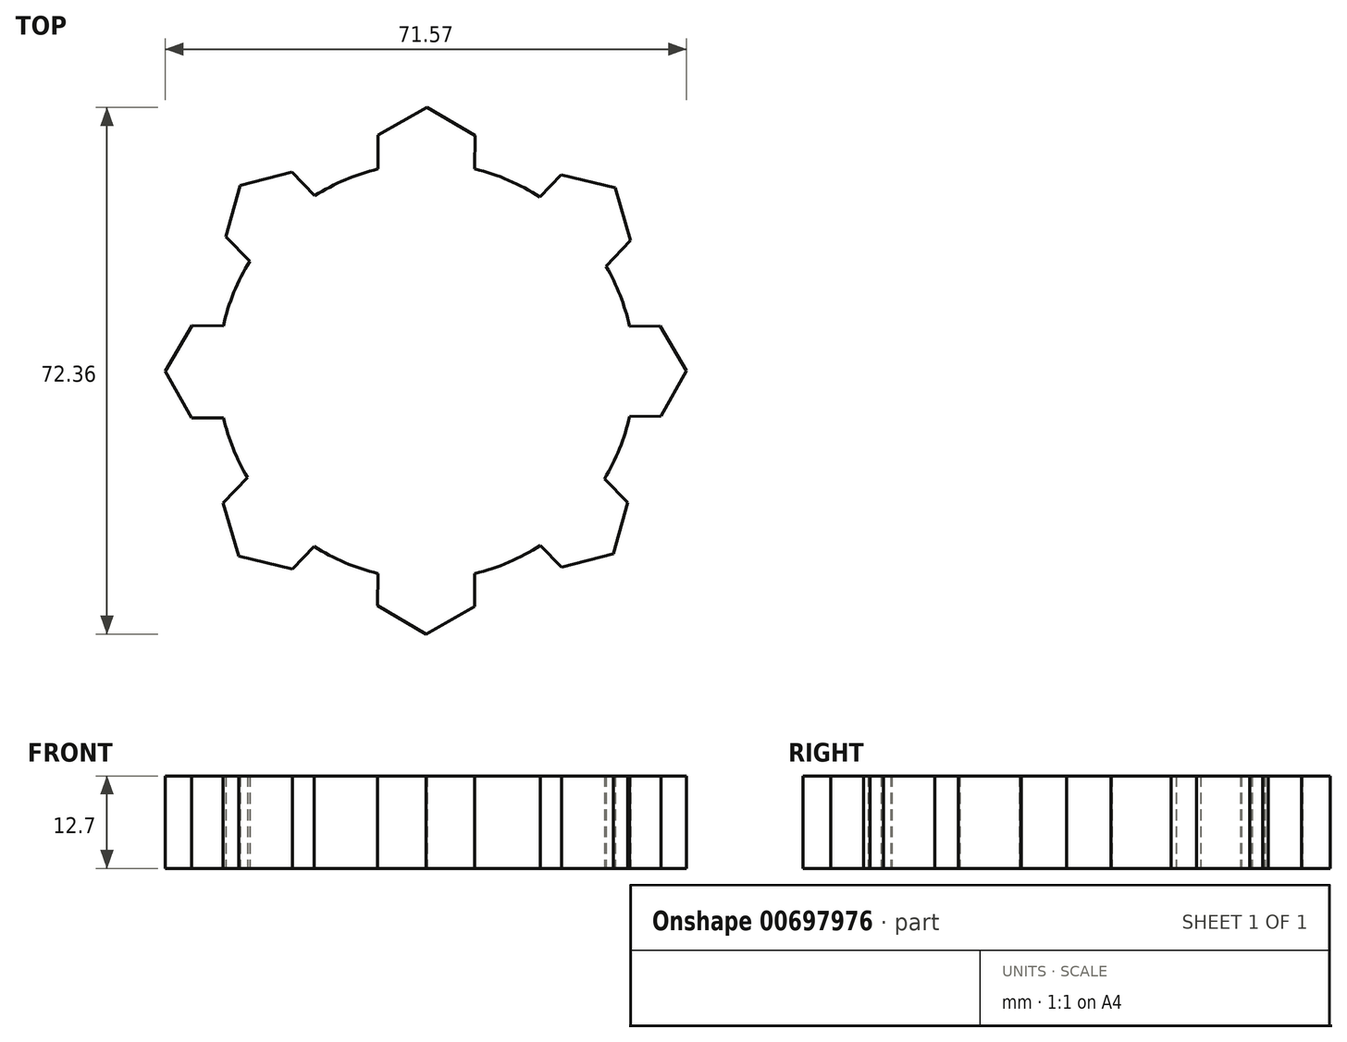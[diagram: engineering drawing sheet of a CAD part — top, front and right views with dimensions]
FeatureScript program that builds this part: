
annotation { "Feature Type Name" : "Feature", "Feature Type Description" : "" }
export const myFeature = defineFeature(function(context is Context, id is Id, definition is map)
    precondition{}
    {
        {
            var Q0;
            Q0=qCreatedBy(makeId("Top.planeOp"),FACE);
            var sketch = newSketch(context, id + "F0", { "sketchPlane" : qUnion([Q0])});
            skCircle(sketch, "E0", {"center": v(0, 0) * mm, "radius": 28.58 * mm});
            skCircle(sketch, "E1.cCircle", {"center": v(0, 28.58) * mm, "radius": 6.65 * mm, "construction": true});
            skLineSegment(sketch, "E1.0", {"start": v(0.06, 36.25) * mm, "end": v(6.68, 32.36) * mm});
            skLineSegment(sketch, "E1.1", {"start": v(6.68, 32.36) * mm, "end": v(6.62, 24.68) * mm});
            skLineSegment(sketch, "E1.2", {"start": v(6.62, 24.68) * mm, "end": v(-0.06, 20.9) * mm});
            skLineSegment(sketch, "E1.3", {"start": v(-0.06, 20.9) * mm, "end": v(-6.68, 24.8) * mm});
            skLineSegment(sketch, "E1.4", {"start": v(-6.68, 24.8) * mm, "end": v(-6.62, 32.47) * mm});
            skLineSegment(sketch, "E1.5", {"start": v(-6.62, 32.47) * mm, "end": v(0.06, 36.25) * mm});
            skPoint(sketch, "E1.0.midPoint", {"position": v(3.37, 34.3) * mm});
            skCircle(sketch, "E2.cCircle", {"center": v(0, -28.43) * mm, "radius": 6.65 * mm, "construction": true});
            skLineSegment(sketch, "E2.0", {"start": v(0.06, -20.75) * mm, "end": v(6.68, -24.64) * mm});
            skLineSegment(sketch, "E2.1", {"start": v(6.68, -24.64) * mm, "end": v(6.62, -32.32) * mm});
            skLineSegment(sketch, "E2.2", {"start": v(6.62, -32.32) * mm, "end": v(-0.06, -36.1) * mm});
            skLineSegment(sketch, "E2.3", {"start": v(-0.06, -36.1) * mm, "end": v(-6.68, -32.21) * mm});
            skLineSegment(sketch, "E2.4", {"start": v(-6.68, -32.21) * mm, "end": v(-6.62, -24.53) * mm});
            skLineSegment(sketch, "E2.5", {"start": v(-6.62, -24.53) * mm, "end": v(0.06, -20.75) * mm});
            skPoint(sketch, "E2.0.midPoint", {"position": v(3.37, -22.7) * mm});
            skCircle(sketch, "E3.cCircle", {"center": v(-28.55, -0.08) * mm, "radius": 6.33 * mm, "construction": true});
            skLineSegment(sketch, "E3.0", {"start": v(-21.24, -0.14) * mm, "end": v(-24.95, -6.44) * mm});
            skLineSegment(sketch, "E3.1", {"start": v(-24.95, -6.44) * mm, "end": v(-32.26, -6.38) * mm});
            skLineSegment(sketch, "E3.2", {"start": v(-32.26, -6.38) * mm, "end": v(-35.86, -0.01) * mm});
            skLineSegment(sketch, "E3.3", {"start": v(-35.86, -0.01) * mm, "end": v(-32.15, 6.28) * mm});
            skLineSegment(sketch, "E3.4", {"start": v(-32.15, 6.28) * mm, "end": v(-24.84, 6.22) * mm});
            skLineSegment(sketch, "E3.5", {"start": v(-24.84, 6.22) * mm, "end": v(-21.24, -0.14) * mm});
            skCircle(sketch, "E4.cCircle", {"center": v(28.58, 0) * mm, "radius": 6.18 * mm, "construction": true});
            skLineSegment(sketch, "E4.0", {"start": v(35.71, 0.06) * mm, "end": v(32.2, -6.15) * mm});
            skLineSegment(sketch, "E4.1", {"start": v(32.2, -6.15) * mm, "end": v(25.05, -6.21) * mm});
            skLineSegment(sketch, "E4.2", {"start": v(25.05, -6.21) * mm, "end": v(21.44, -0.06) * mm});
            skLineSegment(sketch, "E4.3", {"start": v(21.44, -0.06) * mm, "end": v(24.96, 6.15) * mm});
            skLineSegment(sketch, "E4.4", {"start": v(24.96, 6.15) * mm, "end": v(32.1, 6.21) * mm});
            skLineSegment(sketch, "E4.5", {"start": v(32.1, 6.21) * mm, "end": v(35.71, 0.06) * mm});
            skCircle(sketch, "E5.cCircle", {"center": v(20.66, 19.74) * mm, "radius": 6.57 * mm, "construction": true});
            skLineSegment(sketch, "E5.0", {"start": v(25.9, 25.23) * mm, "end": v(28.04, 17.95) * mm});
            skLineSegment(sketch, "E5.1", {"start": v(28.04, 17.95) * mm, "end": v(22.8, 12.46) * mm});
            skLineSegment(sketch, "E5.2", {"start": v(22.8, 12.46) * mm, "end": v(15.43, 14.24) * mm});
            skLineSegment(sketch, "E5.3", {"start": v(15.43, 14.24) * mm, "end": v(13.29, 21.53) * mm});
            skLineSegment(sketch, "E5.4", {"start": v(13.29, 21.53) * mm, "end": v(18.53, 27.02) * mm});
            skLineSegment(sketch, "E5.5", {"start": v(18.53, 27.02) * mm, "end": v(25.9, 25.23) * mm});
            skCircle(sketch, "E6.cCircle", {"center": v(20.54, -19.87) * mm, "radius": 6.33 * mm, "construction": true});
            skLineSegment(sketch, "E6.0", {"start": v(25.66, -25.08) * mm, "end": v(18.58, -26.9) * mm});
            skLineSegment(sketch, "E6.1", {"start": v(18.58, -26.9) * mm, "end": v(13.46, -21.7) * mm});
            skLineSegment(sketch, "E6.2", {"start": v(13.46, -21.7) * mm, "end": v(15.41, -14.65) * mm});
            skLineSegment(sketch, "E6.3", {"start": v(15.41, -14.65) * mm, "end": v(22.5, -12.82) * mm});
            skLineSegment(sketch, "E6.4", {"start": v(22.5, -12.82) * mm, "end": v(27.62, -18.03) * mm});
            skLineSegment(sketch, "E6.5", {"start": v(27.62, -18.03) * mm, "end": v(25.66, -25.08) * mm});
            skCircle(sketch, "E7.cCircle", {"center": v(-20.44, 20.3) * mm, "radius": 6.33 * mm, "construction": true});
            skLineSegment(sketch, "E7.0", {"start": v(-15.32, 15.09) * mm, "end": v(-22.4, 13.26) * mm});
            skLineSegment(sketch, "E7.1", {"start": v(-22.4, 13.26) * mm, "end": v(-27.52, 18.47) * mm});
            skLineSegment(sketch, "E7.2", {"start": v(-27.52, 18.47) * mm, "end": v(-25.57, 25.52) * mm});
            skLineSegment(sketch, "E7.3", {"start": v(-25.57, 25.52) * mm, "end": v(-18.49, 27.35) * mm});
            skLineSegment(sketch, "E7.4", {"start": v(-18.49, 27.35) * mm, "end": v(-13.36, 22.13) * mm});
            skLineSegment(sketch, "E7.5", {"start": v(-13.36, 22.13) * mm, "end": v(-15.32, 15.09) * mm});
            skCircle(sketch, "E8.cCircle", {"center": v(-20.55, -19.9) * mm, "radius": 6.57 * mm, "construction": true});
            skLineSegment(sketch, "E8.0", {"start": v(-15.3, -14.4) * mm, "end": v(-13.17, -21.68) * mm});
            skLineSegment(sketch, "E8.1", {"start": v(-13.17, -21.68) * mm, "end": v(-18.4, -27.17) * mm});
            skLineSegment(sketch, "E8.2", {"start": v(-18.4, -27.17) * mm, "end": v(-25.78, -25.39) * mm});
            skLineSegment(sketch, "E8.3", {"start": v(-25.78, -25.39) * mm, "end": v(-27.92, -18.1) * mm});
            skLineSegment(sketch, "E8.4", {"start": v(-27.92, -18.1) * mm, "end": v(-22.68, -12.61) * mm});
            skLineSegment(sketch, "E8.5", {"start": v(-22.68, -12.61) * mm, "end": v(-15.3, -14.4) * mm});
            skSolve(sketch);
        }
        {
            var Q0;
            {var subQ1=sQuery(id+"F0.wireOp",EDGE,"E8.2");Q0=makeQuery(id+"F0.imprint","IMPRINT",FACE,{"disambiguationData":[TD([[makeQuery(id+"F0.imprint","IMPRINT",EDGE,{"derivedFrom":subQ1}),-1.0]])]});}
            var Q1;
            {var subQ1=sQuery(id+"F0.wireOp",EDGE,"E3.2");Q1=makeQuery(id+"F0.imprint","IMPRINT",FACE,{"disambiguationData":[TD([[makeQuery(id+"F0.imprint","IMPRINT",EDGE,{"derivedFrom":subQ1}),-1.0]])]});}
            var Q2;
            {var subQ1=sQuery(id+"F0.wireOp",EDGE,"E7.2");Q2=makeQuery(id+"F0.imprint","IMPRINT",FACE,{"disambiguationData":[TD([[makeQuery(id+"F0.imprint","IMPRINT",EDGE,{"derivedFrom":subQ1}),-1.0]])]});}
            var Q3;
            {var subQ5=sQuery(id+"F0.wireOp",EDGE,"E1.0");Q3=makeQuery(id+"F0.imprint","IMPRINT",FACE,{"disambiguationData":[TD([[makeQuery(id+"F0.imprint","IMPRINT",EDGE,{"derivedFrom":subQ5}),-1.0]])]});}
            var Q4;
            {var subQ5=sQuery(id+"F0.wireOp",EDGE,"E5.0");Q4=makeQuery(id+"F0.imprint","IMPRINT",FACE,{"disambiguationData":[TD([[makeQuery(id+"F0.imprint","IMPRINT",EDGE,{"derivedFrom":subQ5}),-1.0]])]});}
            var Q5;
            {var subQ5=sQuery(id+"F0.wireOp",EDGE,"E4.0");Q5=makeQuery(id+"F0.imprint","IMPRINT",FACE,{"disambiguationData":[TD([[makeQuery(id+"F0.imprint","IMPRINT",EDGE,{"derivedFrom":subQ5}),-1.0]])]});}
            var Q6;
            {var subQ5=sQuery(id+"F0.wireOp",EDGE,"E6.0");Q6=makeQuery(id+"F0.imprint","IMPRINT",FACE,{"disambiguationData":[TD([[makeQuery(id+"F0.imprint","IMPRINT",EDGE,{"derivedFrom":subQ5}),-1.0]])]});}
            var Q7;
            {var subQ1=sQuery(id+"F0.wireOp",EDGE,"E2.2");Q7=makeQuery(id+"F0.imprint","IMPRINT",FACE,{"disambiguationData":[TD([[makeQuery(id+"F0.imprint","IMPRINT",EDGE,{"derivedFrom":subQ1}),-1.0]])]});}
            var Q8;
            {var subQ38=sQuery(id+"F0.wireOp",EDGE,"E1.2");Q8=makeQuery(id+"F0.imprint","IMPRINT",FACE,{"disambiguationData":[TD([[makeQuery(id+"F0.imprint","IMPRINT",EDGE,{"derivedFrom":subQ38}),1.0]])]});}
            var Q9;
            {var subQ5=sQuery(id+"F0.wireOp",EDGE,"E2.0");Q9=makeQuery(id+"F0.imprint","IMPRINT",FACE,{"disambiguationData":[TD([[makeQuery(id+"F0.imprint","IMPRINT",EDGE,{"derivedFrom":subQ5}),-1.0]])]});}
            var Q10;
            {var subQ5=sQuery(id+"F0.wireOp",EDGE,"E8.0");Q10=makeQuery(id+"F0.imprint","IMPRINT",FACE,{"disambiguationData":[TD([[makeQuery(id+"F0.imprint","IMPRINT",EDGE,{"derivedFrom":subQ5}),-1.0]])]});}
            var Q11;
            {var subQ5=sQuery(id+"F0.wireOp",EDGE,"E3.0");Q11=makeQuery(id+"F0.imprint","IMPRINT",FACE,{"disambiguationData":[TD([[makeQuery(id+"F0.imprint","IMPRINT",EDGE,{"derivedFrom":subQ5}),-1.0]])]});}
            var Q12;
            {var subQ0=sQuery(id+"F0.wireOp",EDGE,"E7.0");Q12=makeQuery(id+"F0.imprint","IMPRINT",FACE,{"disambiguationData":[TD([[makeQuery(id+"F0.imprint","IMPRINT",EDGE,{"derivedFrom":subQ0}),-1.0]])]});}
            var Q13;
            {var subQ1=sQuery(id+"F0.wireOp",EDGE,"E1.2");Q13=makeQuery(id+"F0.imprint","IMPRINT",FACE,{"disambiguationData":[TD([[makeQuery(id+"F0.imprint","IMPRINT",EDGE,{"derivedFrom":subQ1}),-1.0]])]});}
            var Q14;
            {var subQ1=sQuery(id+"F0.wireOp",EDGE,"E5.2");Q14=makeQuery(id+"F0.imprint","IMPRINT",FACE,{"disambiguationData":[TD([[makeQuery(id+"F0.imprint","IMPRINT",EDGE,{"derivedFrom":subQ1}),-1.0]])]});}
            var Q15;
            {var subQ1=sQuery(id+"F0.wireOp",EDGE,"E4.2");Q15=makeQuery(id+"F0.imprint","IMPRINT",FACE,{"disambiguationData":[TD([[makeQuery(id+"F0.imprint","IMPRINT",EDGE,{"derivedFrom":subQ1}),-1.0]])]});}
            var Q16;
            {var subQ1=sQuery(id+"F0.wireOp",EDGE,"E6.2");Q16=makeQuery(id+"F0.imprint","IMPRINT",FACE,{"disambiguationData":[TD([[makeQuery(id+"F0.imprint","IMPRINT",EDGE,{"derivedFrom":subQ1}),-1.0]])]});}
            extrude(context, id + "F1", {"entities" : qUnion([Q0, Q1, Q2, Q3, Q4, Q5, Q6, Q7, Q8, Q9, Q10, Q11, Q12, Q13, Q14, Q15, Q16]), "depth" : 12.7 * mm, "offsetDistance" : 25.4 * mm});
        }
    });
